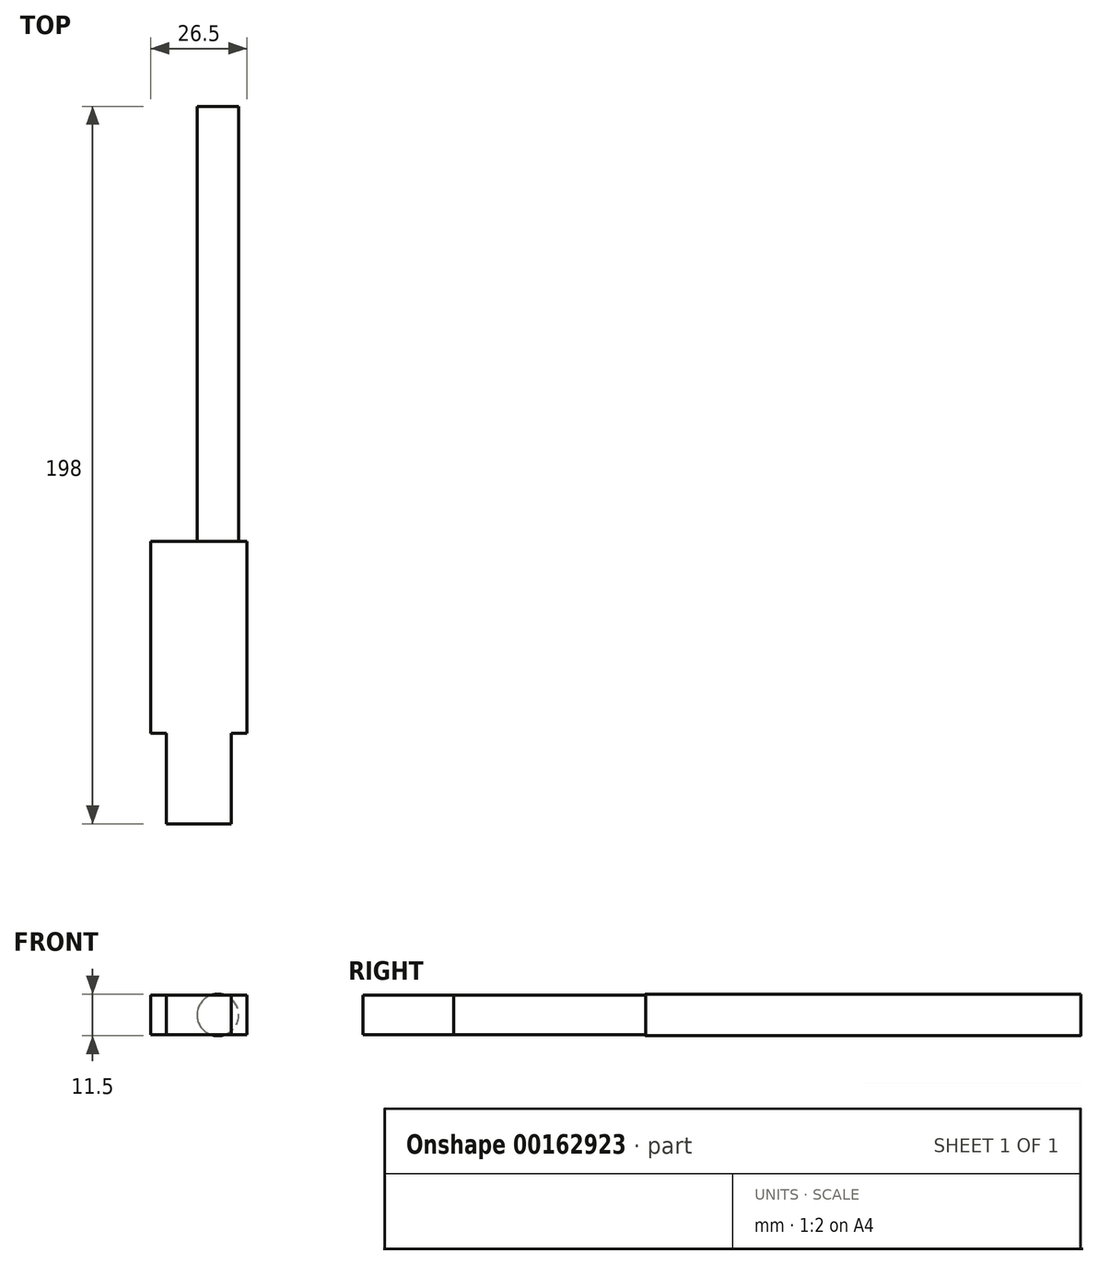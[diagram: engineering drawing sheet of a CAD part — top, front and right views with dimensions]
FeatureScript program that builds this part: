
annotation { "Feature Type Name" : "Feature", "Feature Type Description" : "" }
export const myFeature = defineFeature(function(context is Context, id is Id, definition is map)
    precondition{}
    {
        {
            var Q0;
            Q0=qCreatedBy(makeId("Top.planeOp"),FACE);
            var sketch = newSketch(context, id + "F0", { "sketchPlane" : qUnion([Q0])});
            skLineSegment(sketch, "E0.bottom", {"start": v(13.25, 26.5) * mm, "end": v(-13.25, 26.5) * mm});
            skLineSegment(sketch, "E0.top", {"start": v(13.25, -26.5) * mm, "end": v(-13.25, -26.5) * mm});
            skLineSegment(sketch, "E0.left", {"start": v(13.25, 26.5) * mm, "end": v(13.25, -26.5) * mm});
            skLineSegment(sketch, "E0.right", {"start": v(-13.25, 26.5) * mm, "end": v(-13.25, -26.5) * mm});
            skPoint(sketch, "E0.middle", {"position": v(0, 0) * mm});
            skSolve(sketch);
        }
        {
            var Q0;
            Q0=makeQuery(id+"F0.imprint","IMPRINT",FACE,{"disambiguationData":[TD([[makeQuery(id+"F0.imprint","IMPRINT",EDGE,{"derivedFrom":sQuery(id+"F0.wireOp",EDGE,"E0.bottom")}),1.0]])]});
            extrude(context, id + "F1", {"entities" : qUnion([Q0]), "depth" : 11 * mm});
        }
        {
            var Q0;
            Q0=makeQuery(id+"F1.opExtrude","SWEPT_FACE",FACE,{"disambiguationData":[OSD([sQuery(id+"F0.wireOp",EDGE,"E0.bottom")])]});
            var sketch = newSketch(context, id + "F2", { "sketchPlane" : qUnion([Q0])});
            skCircle(sketch, "E1", {"center": v(-5.25, 5.5) * mm, "radius": 5.75 * mm});
            skPoint(sketch, "E1.centerSnap0", {"position": v(13.25, 5.5) * mm});
            skSolve(sketch);
        }
        {
            var Q0;
            Q0 = qSketchRegion(id + "F2", true);
            extrude(context, id + "F3", {"entities" : qUnion([Q0]), "operationType" : NewBodyOperationType.ADD, "depth" : 120 * mm});
        }
        {
            var Q0;
            Q0=makeQuery(id+"F1.opExtrude","SWEPT_FACE",FACE,{"disambiguationData":[OSD([sQuery(id+"F0.wireOp",EDGE,"E0.top")])]});
            var sketch = newSketch(context, id + "F4", { "sketchPlane" : qUnion([Q0])});
            skLineSegment(sketch, "E2.bottom", {"start": v(9, 11) * mm, "end": v(-9, 11) * mm});
            skLineSegment(sketch, "E2.top", {"start": v(9, 0) * mm, "end": v(-9, 0) * mm});
            skLineSegment(sketch, "E2.left", {"start": v(9, 11) * mm, "end": v(9, 0) * mm});
            skLineSegment(sketch, "E2.right", {"start": v(-9, 11) * mm, "end": v(-9, 0) * mm});
            skPoint(sketch, "E2.middle", {"position": v(0, 5.5) * mm});
            skPoint(sketch, "E2.middle.positionSnap0", {"position": v(13.25, 5.5) * mm});
            skPoint(sketch, "E2.middle.positionSnap1", {"position": v(0, 11) * mm});
            skPoint(sketch, "E2.centerSnap0", {"position": v(13.25, 5.5) * mm});
            skPoint(sketch, "E2.centerSnap1", {"position": v(0, 11) * mm});
            skSolve(sketch);
        }
        {
            var Q0;
            Q0 = qSketchRegion(id + "F4", true);
            extrude(context, id + "F5", {"entities" : qUnion([Q0]), "operationType" : NewBodyOperationType.ADD, "depth" : 25 * mm});
        }
    });
